# Revit family: DimensionalLumber-Plates_Humboldt
name_source: partatom
category: Structural Framing
units: mm (PartAtom-declared; Revit-internal decimal feet)

## family parameters
Always export as geometry = No
Always vertical = Yes
Classification Number = 23.25.30.11.14.14
Cut with Voids When Loaded = No
Material for Model Behavior = Wood
Section Shape = Not Defined
Shared = No
Show family pre-cut in plan views = Yes

## types (56) — shared parameters
Assembly Code = B1010340
Bending (Fb) = 725
Compression (Parallel) = 700
Compression (Perpendicular) = 425
Description = Humboldt 1X4 - Smooth Grain Dimensional Plate
Fire Rating = -
Green Building-LEED = http://www.arcat.com
Keynote = 06 13 00
Lumber Grade = No. 2 Open Grain (OG)No. 2 Open Grain (OG)
Manufacturer = Humboldt Redwood
Manufacturer Fax = (707) 764-4444 � Fax
Manufacturer Website = http://www.getredwood.com
Model = 1X4
Modulus of Elasticity (MOE) = 1
Product Data = -
Revision = R1_04-2017
Sales Information = http://www.getredwood.com
Send Message = http://www.getredwood.com
Shear (Fv) = 160
Specification = http://www.arcat.com
Tension (Ft) = 425
Test Data = http://www.arcat.com
Type Comments = -
URL = http://www.arcat.com
zero-valued in all types: Cost, Expected Lifespan (Years)

## per-type parameters (varying)
| type | Structural Material | b | d |
| Douglas Fir - Rough - Full Sawn - 8X8 | Humboldt Douglas Fir | 0' - 8" | 0' - 8" |
| Douglas Fir - Rough - Full Sawn - 6X12 | Humboldt Douglas Fir | 1' - 0" | 0' - 6" |
| Douglas Fir - Rough - Full Sawn - 6X10 | Humboldt Douglas Fir | 0' - 10" | 0' - 6" |
| Douglas Fir - Rough - Full Sawn - 6X8 | Humboldt Douglas Fir | 0' - 8" | 0' - 6" |
| Douglas Fir - Rough - Full Sawn - 6X6 | Humboldt Douglas Fir | 0' - 6" | 0' - 6" |
| Douglas Fir - Rough - Full Sawn - 4X8 | Humboldt Douglas Fir | 0' - 7 7/8" | 0' - 3 3/4" |
| Douglas Fir - Rough - Full Sawn - 4X6 | Humboldt Douglas Fir | 0' - 5 7/8" | 0' - 3 3/4" |
| Douglas Fir - Rough - 2X6 | Humboldt Douglas Fir | 0' - 5 7/8" | 0' - 1 3/4" |
| Douglas Fir - Rough - 2X4 | Humboldt Douglas Fir | 0' - 3 3/4" | 0' - 1 3/4" |
| Douglas Fir - Surfaced 4 Sides - 6X12 | Humboldt Douglas Fir | 0' - 11 1/2" | 0' - 5 1/2" |
| Douglas Fir - Surfaced 4 Sides - 6X10 | Humboldt Douglas Fir | 0' - 9 1/2" | 0' - 5 1/2" |
| Douglas Fir - Surfaced 4 Sides - 6X8 | Humboldt Douglas Fir | 0' - 7 1/2" | 0' - 5 1/2" |
| Douglas Fir - Surfaced 4 Sides - 6X6 | Humboldt Douglas Fir | 0' - 5 1/2" | 0' - 5 1/2" |
| Douglas Fir - Surfaced 4 Sides - 4X12 | Humboldt Douglas Fir | 0' - 11 1/2" | 0' - 3 9/16" |
| Douglas Fir - Surfaced 4 Sides - 4X10 | Humboldt Douglas Fir | 0' - 9 1/2" | 0' - 3 9/16" |
| Douglas Fir - Surfaced 4 Sides - 4X8 | Humboldt Douglas Fir | 0' - 7 1/2" | 0' - 3 9/16" |
| Douglas Fir - Surfaced 4 Sides - 4X6 | Humboldt Douglas Fir | 0' - 5 5/8" | 0' - 3 9/16" |
| Douglas Fir - Surfaced 4 Sides - 4X4 | Humboldt Douglas Fir | 0' - 3 9/16" | 0' - 3 9/16" |
| Douglas Fir - Surfaced 4 Sides - 3X6 | Humboldt Douglas Fir | 0' - 5 5/8" | 0' - 2 9/16" |
| Douglas Fir - Surfaced 4 Sides - 2X12 | Humboldt Douglas Fir | 0' - 11 1/2" | 0' - 1 1/2" |
| Douglas Fir - Surfaced 4 Sides - 2X10 | Humboldt Douglas Fir | 0' - 9 1/2" | 0' - 1 1/2" |
| Douglas Fir - Surfaced 4 Sides - 2X8 | Humboldt Douglas Fir | 0' - 7 1/2" | 0' - 1 1/2" |
| Douglas Fir - Surfaced 4 Sides - 2X6 | Humboldt Douglas Fir | 0' - 5 1/2" | 0' - 1 1/2" |
| Douglas Fir - Surfaced 4 Sides - 2X4 | Humboldt Douglas Fir | 0' - 3 1/2" | 0' - 1 1/2" |
| Redwood - Rough - 8X8 | Humboldt Redwood | 0' - 7 7/8" | 0' - 7 7/8" |
| Redwood - Rough - 6X12 | Humboldt Redwood | 0' - 11 7/8" | 0' - 5 7/8" |
| Redwood - Rough - 6X10 | Humboldt Redwood | 0' - 9 7/8" | 0' - 5 7/8" |
| Redwood - Rough - 6X8 | Humboldt Redwood | 0' - 7 7/8" | 0' - 5 7/8" |
| Redwood - Rough - 6X6 | Humboldt Redwood | 0' - 5 7/8" | 0' - 5 7/8" |
| Redwood - Rough - 4X12 | Humboldt Redwood | 0' - 11 3/4" | 0' - 3 3/4" |
| Redwood - Rough - 4X10 | Humboldt Redwood | 0' - 9 3/4" | 0' - 3 3/4" |
| Redwood - Rough - 4X8 | Humboldt Redwood | 0' - 7 3/4" | 0' - 3 3/4" |
| Redwood - Rough - 4X6 | Humboldt Redwood | 0' - 5 3/4" | 0' - 3 3/4" |
| Redwood - Rough - 4X4 | Humboldt Redwood | 0' - 3 3/4" | 0' - 3 3/4" |
| Redwood - Surfaced 4 Sides - 8X8 | Humboldt Redwood | 0' - 7 1/2" | 0' - 7 1/2" |
| Redwood - Surfaced 4 Sides - 6X12 | Humboldt Redwood | 0' - 11 1/2" | 0' - 5 1/2" |
| Redwood - Surfaced 4 Sides - 6X10 | Humboldt Redwood | 0' - 9 1/2" | 0' - 5 1/2" |
| Redwood - Surfaced 4 Sides - 6X8 | Humboldt Redwood | 0' - 7 1/2" | 0' - 5 1/2" |
| Redwood - Surfaced 4 Sides - 6X6 | Humboldt Redwood | 0' - 5 1/2" | 0' - 5 1/2" |
| Redwood - Surfaced 4 Sides - 4X12 | Humboldt Redwood | 0' - 11 1/2" | 0' - 3 1/2" |
| Redwood - Surfaced 4 Sides - 4X10 | Humboldt Redwood | 0' - 9 1/2" | 0' - 3 1/2" |
| Redwood - Surfaced 4 Sides - 4X8 | Humboldt Redwood | 0' - 7 1/2" | 0' - 3 1/2" |
| Redwood - Surfaced 4 Sides - 4X6 | Humboldt Redwood | 0' - 5 1/2" | 0' - 3 1/2" |
| Redwood - Surfaced 4 Sides - 4X4 | Humboldt Redwood | 0' - 3 1/2" | 0' - 3 1/2" |
| Redwood - Surfaced 2 sides - 2X12 | Humboldt Redwood | 0' - 11 1/4" | 0' - 1 21/32" |
| Redwood - Surfaced 2 sides - 2X8 | Humboldt Redwood | 0' - 7 1/4" | 0' - 1 21/32" |
| Redwood - Surfaced 2 sides - 2X6 | Humboldt Redwood | 0' - 5 1/2" | 0' - 1 21/32" |
| Redwood - Surfaced 2 sides - 2X4 | Humboldt Redwood | 0' - 3 1/2" | 0' - 1 21/32" |
| Redwood - Rough - 2X12 | Humboldt Redwood | 0' - 11 7/8" | 0' - 1 3/4" |
| Redwood - Rough - 2X8 | Humboldt Redwood | 0' - 7 7/8" | 0' - 1 3/4" |
| Redwood - Rough - 2X6 | Humboldt Redwood | 0' - 5 7/8" | 0' - 1 3/4" |
| Redwood - Rough - 2X4 | Humboldt Redwood | 0' - 3 7/8" | 0' - 1 3/4" |
| Redwood - Surfaced 4 Sides - 2X12 | Humboldt Redwood | 0' - 11 1/4" | 0' - 1 1/2" |
| Redwood - Surfaced 4 Sides - 2X8 | Humboldt Redwood | 0' - 7 1/4" | 0' - 1 1/2" |
| Redwood - Surfaced 4 Sides - 2X6 | Humboldt Redwood | 0' - 5 1/2" | 0' - 1 1/2" |
| Redwood - Surfaced 4 Sides - 2X4 | Humboldt Redwood | 0' - 3 1/2" | 0' - 1 1/2" |

## geometry (parser evidence)
native form markers: Sweep x2
no freeform markers — native parametric forms only
